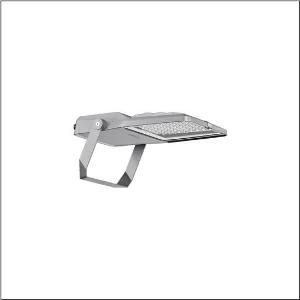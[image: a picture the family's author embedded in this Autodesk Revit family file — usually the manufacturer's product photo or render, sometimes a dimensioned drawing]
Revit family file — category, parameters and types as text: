
# Revit family: floodlight_fl_21_mini___pl64_5xa7775b2e1a_35e6
name_source: partatom
category: Lighting Fixtures
units: mm (PartAtom-declared; Revit-internal decimal feet)

## family parameters
Cut with Voids When Loaded = No
Host = Face
Light Source = No
Part Type = Normal
Room Calculation Point = No
Round Connector Dimension = Use Diameter
Shared = No

## types (1)
- --- (1 x LED, 6010 lm, 45.7 W, 3000K)
    Apparent Load = 46 VA
    CIE Flux Codes = 28 80 98 100 100
    Color Rendering = 70
    Color Temperature = 3000K
    Default Elevation = 1800 mm
    Description = Floodlight FL 21 mini, floodlight, primary light control with lens, of PMMA, primary optical cover: protective disc, of toughened safety glass, transparent, light distribution: PL64, light emission: direct distribution, installation type: surface-mounted, LED, High Power LED, rated luminous flux: 6.010lm, luminous efficacy: 132lm/W, light colour: 730, colour temperature: 3000K, control: flexible luminous flux parameterisation, time-dependent luminous flux control, constant luminous flux control, overheat protection, presetting dimming logarithmic, with terminal, 6-pole, mains connection: 220..240V, AC, 50/60Hz, start of lifetime: 46W, end of service life: 48W, reduction: 22W, luminaire housing, of diecast aluminium, powder-coated, Siteco® metallic grey (DB 702S), corrosivity category C5 mid according to DIN EN ISO 12944, sealing non-destructively replaceable, mounting bracket, of steel, galvanised, powder-coated, Siteco® metallic grey (DB 702S), Smart Interface above, protection rating (complete): IP66, insulation class (complete): insulation class II (safety insulation), certification: CE, ENEC, VDE, protection symbol: D, impact resistance: IK08, permissible operating ambient temperature: -40..+40°C, permissible operating ambient temperature for outdoor applications: -40..+50°C, standard: DIN EN 12944, LABS conformity tested according to VDMA 24364:2018-05, packaging unit: 1 piece

Light Distribution: PL64
    Height = 70 mm
    Lamp = 1 x LED
    Lamp Light Flux = 6010 lm
    Lamp Power = 45.7 W
    Lamp count = 1
    Length = 485 mm
    Luminous efficacy = 132 lm/W
    Manufacturer = Siteco
    ModVariant = No
    Model = 5XA7775B2E1A
    Number of Poles = 1
    OnlyDefault = Yes
    Power Factor = 1
    Product Name = Floodlight FL 21 mini | PL64
    Product group = floodlight | pylon annexe
    ProductGroupID = 6200
    Protection Class = Protection class II
    Protection Degree = IP 66
    RLX_Detail_Level = 1
    RLX_Emergency_Light_Flux = 0 lm
    RLX_Emergency_Type = 0
    RLX_Emergency_Type_DB = No
    RlxData = <blob elided: 95893 chars, md5=10e248bd>
    Socket = socket
    Standby Power = 0 W
    System Light Flux = 6010 lm
    System Power = 46 W
    Type Comments = factory setting: luminous flux: 100 % | dim-lin: 254 | 463 mA
    Type Image = l_1006845.jpg
    URL = http://relux.com
    VarID = @adj_097877
    Voltage = 0 V
    Weight = 0.00 kg
    Width = 337 mm

## geometry (parser evidence)
native form markers: Blend x4, Sweep x11
no freeform markers — native parametric forms only
